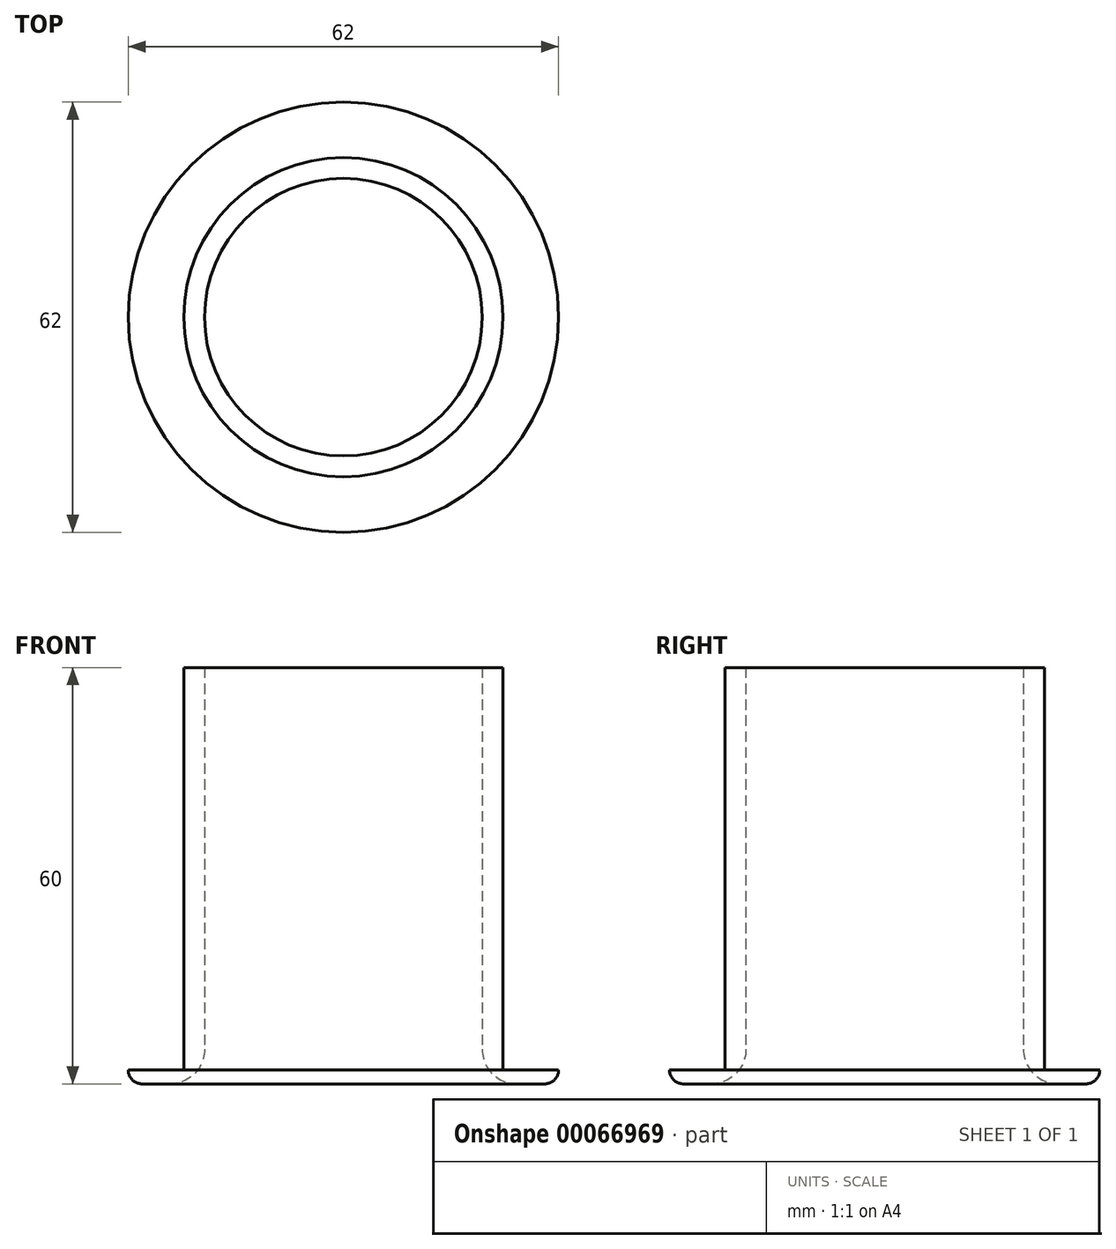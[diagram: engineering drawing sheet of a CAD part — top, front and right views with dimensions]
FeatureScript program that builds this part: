
annotation { "Feature Type Name" : "Feature", "Feature Type Description" : "" }
export const myFeature = defineFeature(function(context is Context, id is Id, definition is map)
    precondition{}
    {
        {
            var Q0;
            Q0=qCreatedBy(makeId("Top.planeOp"),FACE);
            var sketch = newSketch(context, id + "F0", { "sketchPlane" : qUnion([Q0])});
            skCircle(sketch, "E0", {"center": v(0, 0) * mm, "radius": 20 * mm});
            skCircle(sketch, "E1.0", {"center": v(0, 0) * mm, "radius": 23 * mm});
            skCircle(sketch, "E2.0", {"center": v(0, 0) * mm, "radius": 31 * mm});
            skSolve(sketch);
        }
        {
            var Q0;
            Q0=makeQuery(id+"F0.imprint","IMPRINT",FACE,{"disambiguationData":[TD([[makeQuery(id+"F0.imprint","IMPRINT",EDGE,{"derivedFrom":sQuery(id+"F0.wireOp",EDGE,"E0")}),-1.0]])]});
            extrude(context, id + "F1", {"entities" : qUnion([Q0]), "depth" : 60 * mm});
        }
        {
            var Q0;
            Q0=makeQuery(id+"F0.imprint","IMPRINT",FACE,{"disambiguationData":[TD([[makeQuery(id+"F0.imprint","IMPRINT",EDGE,{"derivedFrom":sQuery(id+"F0.wireOp",EDGE,"E1.0")}),-1.0]])]});
            extrude(context, id + "F2", {"entities" : qUnion([Q0]), "operationType" : NewBodyOperationType.ADD, "depth" : 2 * mm});
        }
        {
            var Q0;
            Q0=makeQuery(id+"F2.opExtrude","CAP_EDGE",EDGE,{"disambiguationData":[OSD([sQuery(id+"F0.wireOp",EDGE,"E2.0")])],"isStart":true});
            fillet(context, id + "F3", {"entities" : qUnion([Q0]), "radius" : 2 * mm, "allowEdgeOverflow" : false});
        }
        {
            var Q0;
            Q0=makeQuery(id+"F1.opExtrude","CAP_EDGE",EDGE,{"disambiguationData":[OSD([sQuery(id+"F0.wireOp",EDGE,"E0")])],"isStart":true});
            fillet(context, id + "F4", {"entities" : qUnion([Q0]), "radius" : 5 * mm, "tangentPropagation" : true, "allowEdgeOverflow" : false});
        }
    });
